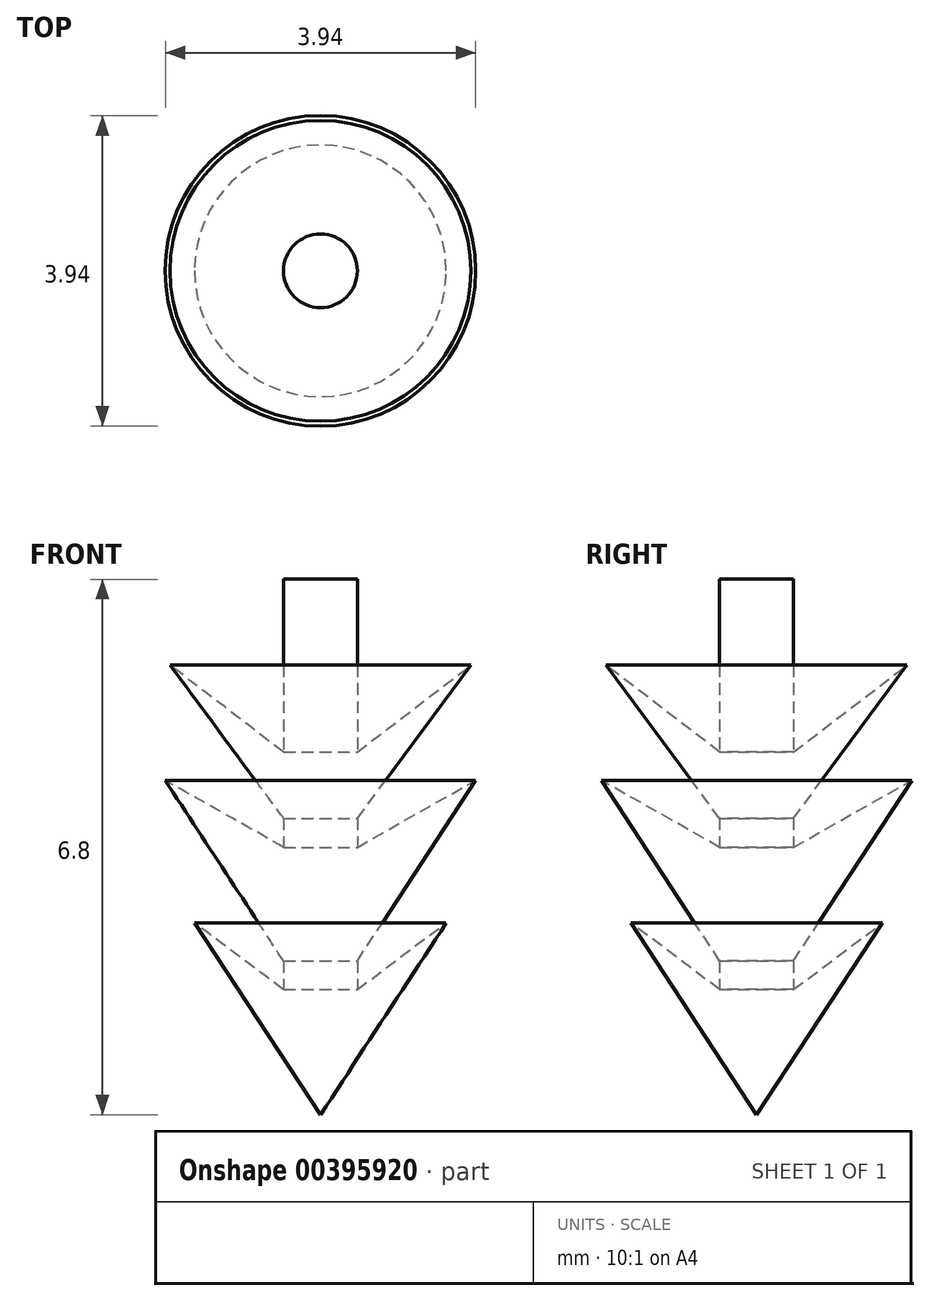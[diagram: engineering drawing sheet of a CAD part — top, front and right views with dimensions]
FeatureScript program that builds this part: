
annotation { "Feature Type Name" : "Feature", "Feature Type Description" : "" }
export const myFeature = defineFeature(function(context is Context, id is Id, definition is map)
    precondition{}
    {
        {
            var Q0;
            Q0=qCreatedBy(makeId("Front.planeOp"),FACE);
            var sketch = newSketch(context, id + "F0", { "sketchPlane" : qUnion([Q0])});
            skLineSegment(sketch, "E0", {"start": v(0, -8.64) * mm, "end": v(-1.6, -6.2) * mm});
            skLineSegment(sketch, "E1", {"start": v(-1.6, -6.2) * mm, "end": v(-0.47, -7.05) * mm});
            skLineSegment(sketch, "E2", {"start": v(-0.47, -6.69) * mm, "end": v(-1.97, -4.4) * mm});
            skLineSegment(sketch, "E3", {"start": v(-1.97, -4.4) * mm, "end": v(-0.47, -5.24) * mm});
            skLineSegment(sketch, "E4", {"start": v(-0.47, -4.88) * mm, "end": v(-1.91, -2.93) * mm});
            skLineSegment(sketch, "E5", {"start": v(-1.91, -2.93) * mm, "end": v(-0.47, -4.03) * mm});
            skLineSegment(sketch, "E6", {"start": v(0, -8.64) * mm, "end": v(0, -1.84) * mm});
            skPoint(sketch, "E7.start.orphan", {"position": v(1.5, -2.93) * mm});
            skPoint(sketch, "E8.end.orphan", {"position": v(1.5, -4.4) * mm});
            skPoint(sketch, "E9.end.orphan", {"position": v(1.5, -6.2) * mm});
            skLineSegment(sketch, "E10", {"start": v(0, -1.84) * mm, "end": v(-0.47, -1.84) * mm});
            skLineSegment(sketch, "E11", {"start": v(-0.47, -1.84) * mm, "end": v(-0.47, -4.03) * mm});
            skLineSegment(sketch, "E12.trimOffspring", {"start": v(-0.47, -4.88) * mm, "end": v(-0.47, -5.24) * mm});
            skLineSegment(sketch, "E13.trimOffspring", {"start": v(-0.47, -6.69) * mm, "end": v(-0.47, -7.05) * mm});
            skPoint(sketch, "E14.orphan", {"position": v(0, -5.5) * mm});
            skPoint(sketch, "E15.orphan", {"position": v(0, -7.4) * mm});
            skPoint(sketch, "E16.orphan", {"position": v(0, -4.4) * mm});
            skSolve(sketch);
        }
        {
            var Q0;
            Q0=makeQuery(id+"F0.imprint","IMPRINT",FACE,{"disambiguationData":[TD([[makeQuery(id+"F0.imprint","IMPRINT",EDGE,{"derivedFrom":sQuery(id+"F0.wireOp",EDGE,"E0")}),-1.0]])]});
            var Q1;
            Q1=sQuery(id+"F0.wireOp",EDGE,"E6");
            revolve(context, id + "F1", {"entities" : qUnion([Q0]), "axis" : qUnion([Q1]), "revolveType" : RevolveType.FULL});
        }
    });
